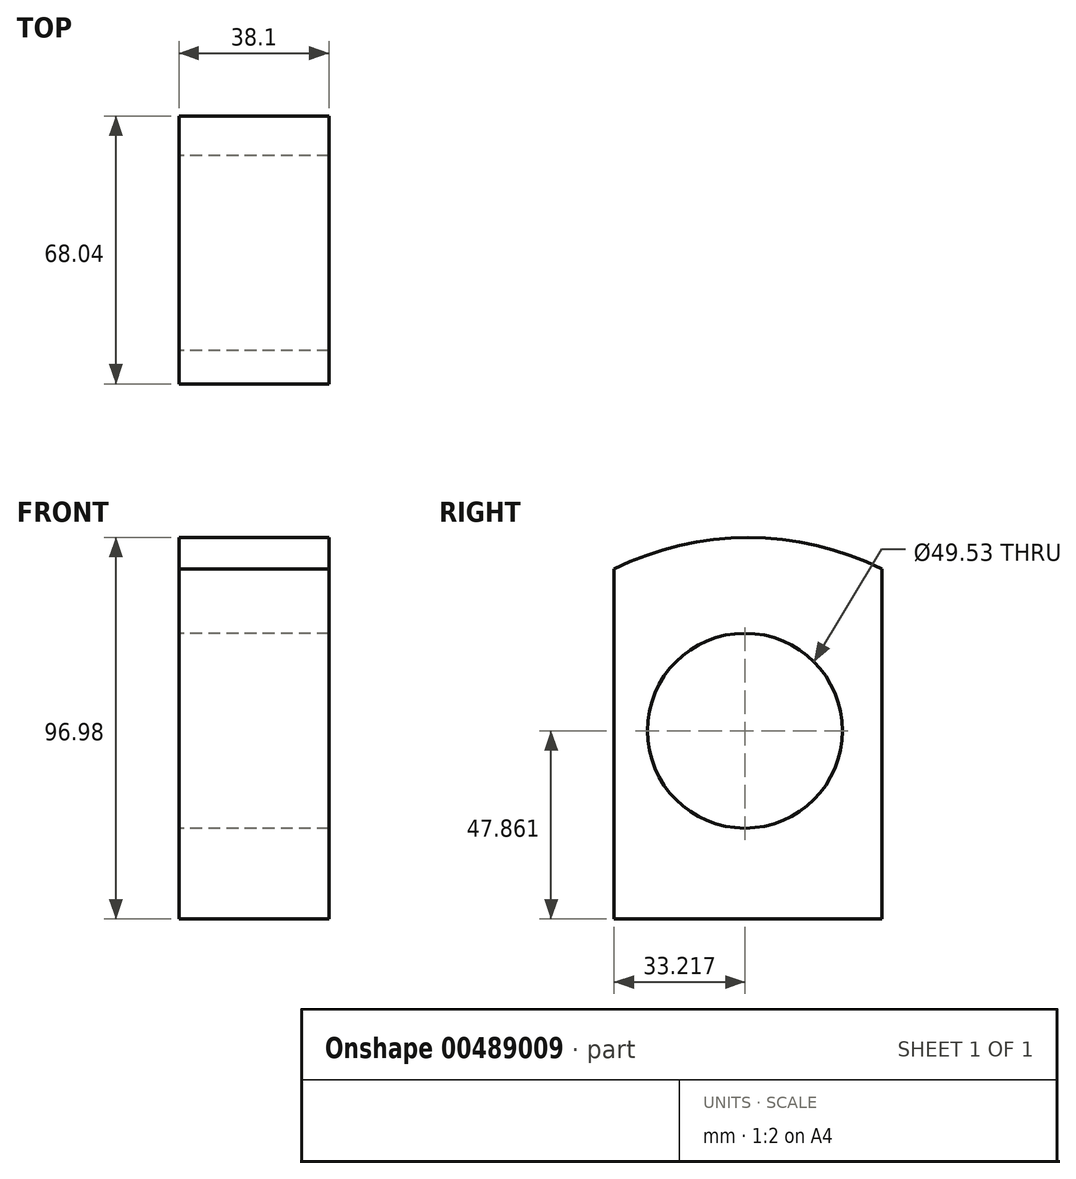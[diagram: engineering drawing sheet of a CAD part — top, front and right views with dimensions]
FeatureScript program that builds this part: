
annotation { "Feature Type Name" : "Feature", "Feature Type Description" : "" }
export const myFeature = defineFeature(function(context is Context, id is Id, definition is map)
    precondition{}
    {
        {
            var Q0;
            Q0=qCreatedBy(makeId("Right.planeOp"),FACE);
            var sketch = newSketch(context, id + "F0", { "sketchPlane" : qUnion([Q0])});
            skLineSegment(sketch, "E0.bottom", {"start": v(0, 70.03) * mm, "end": v(-68.04, 70.03) * mm});
            skLineSegment(sketch, "E0.top", {"start": v(0, -18.87) * mm, "end": v(-68.04, -18.87) * mm});
            skLineSegment(sketch, "E0.left", {"start": v(0, 70.03) * mm, "end": v(0, -18.87) * mm});
            skLineSegment(sketch, "E0.right", {"start": v(-68.04, 70.03) * mm, "end": v(-68.04, -18.87) * mm});
            skArc(sketch, "E1", {"start": v(0, 70.03) * mm, "mid": v(-34.02, 78.1) * mm, "end": v(-68.04, 70.03) * mm});
            skCircle(sketch, "E2", {"center": v(-34.82, 29) * mm, "radius": 24.76 * mm});
            skSolve(sketch);
        }
        {
            var Q0;
            Q0 = qSketchRegion(id + "F0", true);
            extrude(context, id + "F1", {"entities" : qUnion([Q0]), "depth" : 38.1 * mm});
        }
    });
